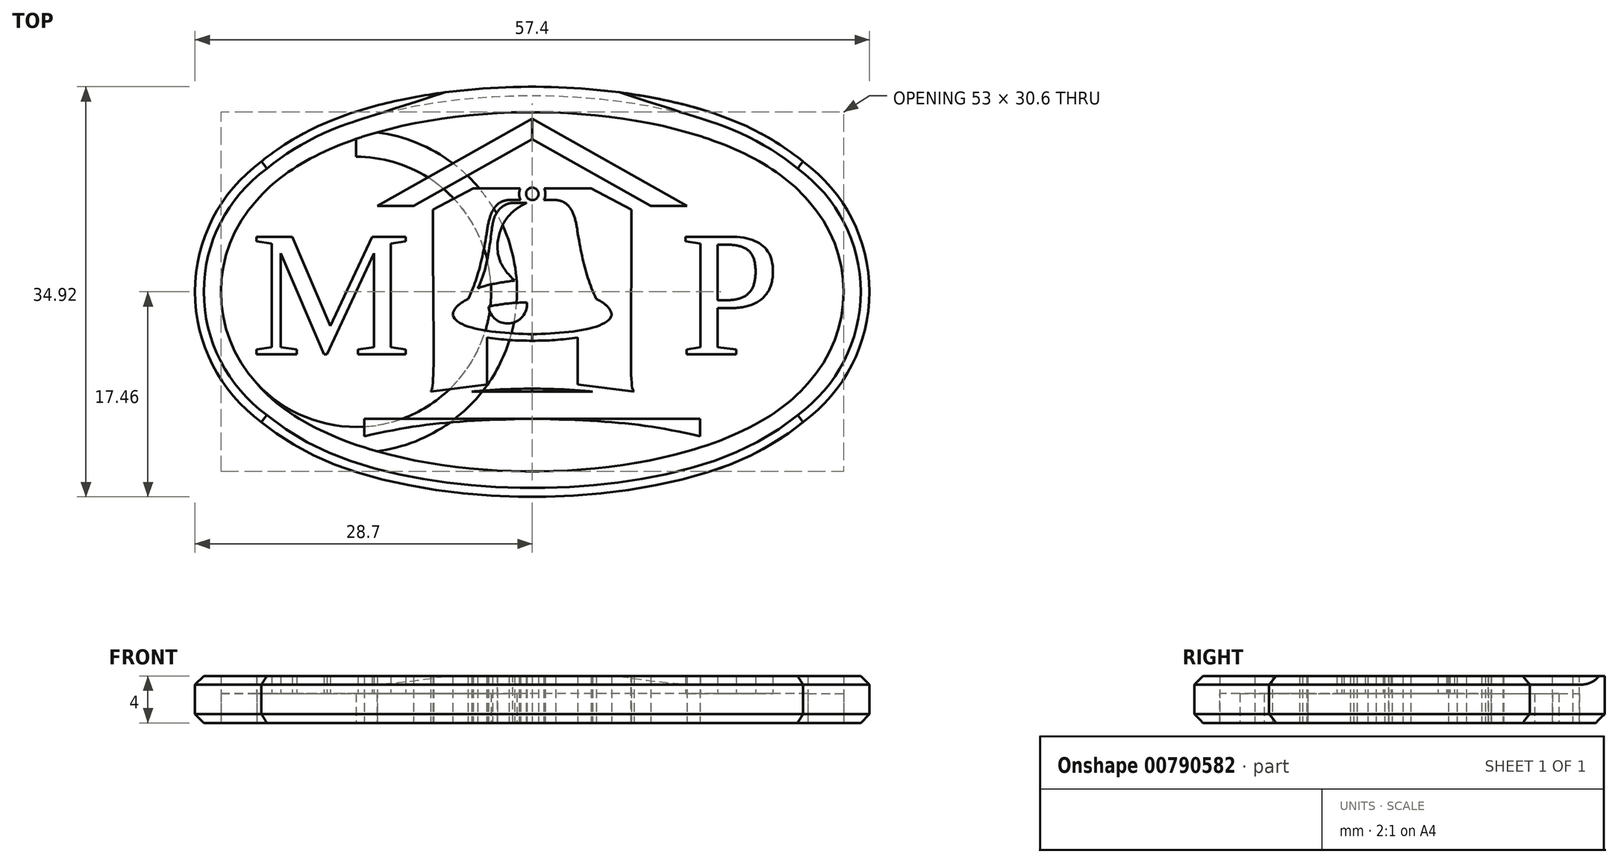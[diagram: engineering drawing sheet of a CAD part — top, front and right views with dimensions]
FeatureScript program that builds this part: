
annotation { "Feature Type Name" : "Feature", "Feature Type Description" : "" }
export const myFeature = defineFeature(function(context is Context, id is Id, definition is map)
    precondition{}
    {
        {
            var Q0;
            Q0=qCreatedBy(makeId("Top.planeOp"),FACE);
            var sketch = newSketch(context, id + "F0", { "sketchPlane" : qUnion([Q0])});
            skLineSegment(sketch, "E0", {"start": v(0, 0) * mm, "end": v(15, 0) * mm});
            skCircle(sketch, "E1", {"center": v(15, 0) * mm, "radius": 11.5 * mm});
            skCircle(sketch, "E2.MirrorC", {"center": v(-15, 0) * mm, "radius": 11.5 * mm});
            skLineSegment(sketch, "E3", {"start": v(15, 0) * mm, "end": v(15, -11.5) * mm});
            skLineSegment(sketch, "E4", {"start": v(15, 0) * mm, "end": v(15, 7.8) * mm});
            skLineSegment(sketch, "E5", {"start": v(15, 7.8) * mm, "end": v(23.45, 7.8) * mm});
            skLineSegment(sketch, "E6.MirrorCS", {"start": v(-15, 0) * mm, "end": v(-15, 7.8) * mm});
            skLineSegment(sketch, "E7.MirrorCS", {"start": v(-15, 7.8) * mm, "end": v(-23.45, 7.8) * mm});
            skLineSegment(sketch, "E8", {"start": v(15, 7.8) * mm, "end": v(15, 17.8) * mm});
            skLineSegment(sketch, "E9.MirrorCS", {"start": v(-15, 7.8) * mm, "end": v(-15, 17.8) * mm});
            skFitSpline(sketch, "E10", {"points": [v(23.45, 7.8) * mm, v(-23.45, 7.8) * mm], "startDerivative": vector(-25.35, 30) * mm, "endDerivative": vector(-25.35, -30) * mm});
            skFitSpline(sketch, "E11.MirrorCS", {"points": [v(23.45, -7.8) * mm, v(-23.45, -7.8) * mm], "startDerivative": vector(-25.35, -30) * mm, "endDerivative": vector(-25.35, 30) * mm});
            skFitSpline(sketch, "E12.0", {"points": [v(24.98, 9.1) * mm, v(24.36, 9.83) * mm, v(22.94, 11.18) * mm, v(19.56, 13.43) * mm, v(14.48, 15.51) * mm, v(7.47, 16.98) * mm, v(0, 17.46) * mm, v(-7.47, 16.98) * mm, v(-14.48, 15.51) * mm, v(-19.56, 13.43) * mm, v(-22.94, 11.18) * mm, v(-24.36, 9.83) * mm, v(-24.98, 9.1) * mm]});
            skFitSpline(sketch, "E13.0", {"points": [v(24.98, -9.1) * mm, v(24.36, -9.83) * mm, v(22.94, -11.18) * mm, v(19.56, -13.43) * mm, v(14.48, -15.51) * mm, v(7.47, -16.98) * mm, v(0, -17.46) * mm, v(-7.47, -16.98) * mm, v(-14.48, -15.51) * mm, v(-19.56, -13.43) * mm, v(-22.94, -11.18) * mm, v(-24.36, -9.83) * mm, v(-24.98, -9.1) * mm]});
            skCircle(sketch, "E14.0", {"center": v(-15, 0) * mm, "radius": 13.7 * mm});
            skCircle(sketch, "E15.0", {"center": v(15, 0) * mm, "radius": 13.7 * mm});
            skSolve(sketch);
        }
        {
            var Q0;
            {var subQ7=sQuery(id+"F0.wireOp",EDGE,"E12.0");var subQ8=sQuery(id+"F0.wireOp",EDGE,"E8");var subQ9=makeQuery(id+"F0.imprint","INTERSECT",VERTEX,{"derivedFrom":[subQ8,subQ7]});Q0=makeQuery(id+"F0.imprint","IMPRINT",FACE,{"disambiguationData":[TD([[makeQuery(id+"F0.imprint","IMPRINT",EDGE,{"disambiguationData":[TD([[subQ9,1.0]])],"derivedFrom":subQ8}),1.0]])]});}
            var Q1;
            {var subQ0=sQuery(id+"F0.wireOp",EDGE,"E10");var subQ3=sQuery(id+"F0.wireOp",EDGE,"E9.MirrorCS");var subQ4=makeQuery(id+"F0.imprint","INTERSECT",VERTEX,{"derivedFrom":[subQ3,subQ0]});Q1=makeQuery(id+"F0.imprint","IMPRINT",FACE,{"disambiguationData":[TD([[makeQuery(id+"F0.imprint","IMPRINT",EDGE,{"disambiguationData":[TD([[subQ4,-1.0]])],"derivedFrom":subQ3}),1.0]])]});}
            var Q2;
            {var subQ0=sQuery(id+"F0.wireOp",EDGE,"E12.0");var subQ1=sQuery(id+"F0.wireOp",EDGE,"E9.MirrorCS");var subQ2=makeQuery(id+"F0.imprint","INTERSECT",VERTEX,{"derivedFrom":[subQ1,subQ0]});Q2=makeQuery(id+"F0.imprint","IMPRINT",FACE,{"disambiguationData":[TD([[makeQuery(id+"F0.imprint","IMPRINT",EDGE,{"disambiguationData":[TD([[subQ2,1.0]])],"derivedFrom":subQ1}),1.0]])]});}
            var Q3;
            {var subQ0=sQuery(id+"F0.wireOp",EDGE,"E15.0");var subQ1=sQuery(id+"F0.wireOp",EDGE,"E11.MirrorCS");var subQ2=makeQuery(id+"F0.imprint","INTERSECT",VERTEX,{"derivedFrom":[subQ1,subQ0]});Q3=makeQuery(id+"F0.imprint","IMPRINT",FACE,{"disambiguationData":[TD([[makeQuery(id+"F0.imprint","IMPRINT",EDGE,{"disambiguationData":[TD([[subQ2,-1.0]])],"derivedFrom":subQ1}),1.0]])]});}
            var Q4;
            {var subQ5=sQuery(id+"F0.wireOp",EDGE,"E10");var subQ6=sQuery(id+"F0.wireOp",EDGE,"E8");var subQ7=makeQuery(id+"F0.imprint","INTERSECT",VERTEX,{"derivedFrom":[subQ6,subQ5]});Q4=makeQuery(id+"F0.imprint","IMPRINT",FACE,{"disambiguationData":[TD([[makeQuery(id+"F0.imprint","IMPRINT",EDGE,{"disambiguationData":[TD([[subQ7,-1.0]])],"derivedFrom":subQ6}),-1.0]])]});}
            var Q5;
            {var subQ0=sQuery(id+"F0.wireOp",EDGE,"E12.0");var subQ1=sQuery(id+"F0.wireOp",EDGE,"E8");var subQ2=makeQuery(id+"F0.imprint","INTERSECT",VERTEX,{"derivedFrom":[subQ1,subQ0]});Q5=makeQuery(id+"F0.imprint","IMPRINT",FACE,{"disambiguationData":[TD([[makeQuery(id+"F0.imprint","IMPRINT",EDGE,{"disambiguationData":[TD([[subQ2,1.0]])],"derivedFrom":subQ1}),-1.0]])]});}
            var Q6;
            {var subQ0=sQuery(id+"F0.wireOp",EDGE,"E10");var subQ1=sQuery(id+"F0.wireOp",EDGE,"E8");var subQ2=makeQuery(id+"F0.imprint","INTERSECT",VERTEX,{"derivedFrom":[subQ1,subQ0]});Q6=makeQuery(id+"F0.imprint","IMPRINT",FACE,{"disambiguationData":[TD([[makeQuery(id+"F0.imprint","IMPRINT",EDGE,{"disambiguationData":[TD([[subQ2,-1.0]])],"derivedFrom":subQ1}),1.0]])]});}
            var Q7;
            {var subQ0=sQuery(id+"F0.wireOp",EDGE,"E10");var subQ1=sQuery(id+"F0.wireOp",EDGE,"E9.MirrorCS");var subQ2=makeQuery(id+"F0.imprint","INTERSECT",VERTEX,{"derivedFrom":[subQ1,subQ0]});Q7=makeQuery(id+"F0.imprint","IMPRINT",FACE,{"disambiguationData":[TD([[makeQuery(id+"F0.imprint","IMPRINT",EDGE,{"disambiguationData":[TD([[subQ2,-1.0]])],"derivedFrom":subQ1}),-1.0]])]});}
            extrude(context, id + "F1", {"entities" : qUnion([Q0, Q1, Q2, Q3, Q4, Q5, Q6, Q7]), "depth" : 4 * mm, "offsetDistance" : 25 * mm});
        }
        {
            var Q0;
            {var subQ4=sQuery(id+"F0.wireOp",EDGE,"E7.MirrorCS");Q0=makeQuery(id+"F0.imprint","IMPRINT",FACE,{"disambiguationData":[TD([[makeQuery(id+"F0.imprint","IMPRINT",EDGE,{"derivedFrom":subQ4}),1.0]])]});}
            var Q1;
            {var subQ0=sQuery(id+"F0.wireOp",EDGE,"E7.MirrorCS");Q1=makeQuery(id+"F0.imprint","IMPRINT",FACE,{"disambiguationData":[TD([[makeQuery(id+"F0.imprint","IMPRINT",EDGE,{"derivedFrom":subQ0}),-1.0]])]});}
            var Q2;
            {var subQ1=sQuery(id+"F0.wireOp",EDGE,"E2.MirrorC");var subQ3=sQuery(id+"F0.wireOp",EDGE,"E9.MirrorCS");var subQ4=makeQuery(id+"F0.imprint","INTERSECT",VERTEX,{"derivedFrom":[subQ1,subQ3]});Q2=makeQuery(id+"F0.imprint","IMPRINT",FACE,{"disambiguationData":[TD([[makeQuery(id+"F0.imprint","IMPRINT",EDGE,{"disambiguationData":[TD([[subQ4,-1.0]])],"derivedFrom":subQ3}),1.0]])]});}
            var Q3;
            {var subQ5=sQuery(id+"F0.wireOp",EDGE,"E11.MirrorCS");var subQ7=sQuery(id+"F0.wireOp",EDGE,"E2.MirrorC");var subQ8=makeQuery(id+"F0.imprint","INTERSECT",VERTEX,{"derivedFrom":[subQ7,subQ5]});Q3=makeQuery(id+"F0.imprint","IMPRINT",FACE,{"disambiguationData":[TD([[makeQuery(id+"F0.imprint","IMPRINT",EDGE,{"disambiguationData":[TD([[subQ8,1.0]])],"derivedFrom":subQ7}),1.0]])]});}
            var Q4;
            {var subQ0=sQuery(id+"F0.wireOp",EDGE,"E15.0");var subQ2=sQuery(id+"F0.wireOp",EDGE,"E10");var subQ3=makeQuery(id+"F0.imprint","INTERSECT",VERTEX,{"derivedFrom":[subQ2,subQ0]});Q4=makeQuery(id+"F0.imprint","IMPRINT",FACE,{"disambiguationData":[TD([[makeQuery(id+"F0.imprint","IMPRINT",EDGE,{"disambiguationData":[TD([[subQ3,-1.0]])],"derivedFrom":subQ2}),1.0]])]});}
            var Q5;
            {var subQ3=sQuery(id+"F0.wireOp",EDGE,"E15.0");var subQ6=sQuery(id+"F0.wireOp",EDGE,"E0");var subQ9=makeQuery(id+"F0.imprint","INTERSECT",VERTEX,{"derivedFrom":[subQ6,subQ3]});Q5=makeQuery(id+"F0.imprint","IMPRINT",FACE,{"disambiguationData":[TD([[makeQuery(id+"F0.imprint","IMPRINT",EDGE,{"disambiguationData":[TD([[subQ9,-1.0]])],"derivedFrom":subQ6}),1.0]])]});}
            var Q6;
            {var subQ0=sQuery(id+"F0.wireOp",EDGE,"E4");Q6=makeQuery(id+"F0.imprint","IMPRINT",FACE,{"disambiguationData":[TD([[makeQuery(id+"F0.imprint","IMPRINT",EDGE,{"derivedFrom":subQ0}),1.0]])]});}
            var Q7;
            {var subQ0=sQuery(id+"F0.wireOp",EDGE,"E3");Q7=makeQuery(id+"F0.imprint","IMPRINT",FACE,{"disambiguationData":[TD([[makeQuery(id+"F0.imprint","IMPRINT",EDGE,{"derivedFrom":subQ0}),-1.0]])]});}
            var Q8;
            {var subQ3=sQuery(id+"F0.wireOp",EDGE,"E15.0");var subQ6=sQuery(id+"F0.wireOp",EDGE,"E0");var subQ8=makeQuery(id+"F0.imprint","INTERSECT",VERTEX,{"derivedFrom":[subQ6,subQ3]});Q8=makeQuery(id+"F0.imprint","IMPRINT",FACE,{"disambiguationData":[TD([[makeQuery(id+"F0.imprint","IMPRINT",EDGE,{"disambiguationData":[TD([[subQ8,-1.0]])],"derivedFrom":subQ6}),-1.0]])]});}
            var Q9;
            {var subQ0=sQuery(id+"F0.wireOp",EDGE,"E5");Q9=makeQuery(id+"F0.imprint","IMPRINT",FACE,{"disambiguationData":[TD([[makeQuery(id+"F0.imprint","IMPRINT",EDGE,{"derivedFrom":subQ0}),1.0]])]});}
            var Q10;
            {var subQ1=sQuery(id+"F0.wireOp",EDGE,"E1");var subQ3=sQuery(id+"F0.wireOp",EDGE,"E8");var subQ4=makeQuery(id+"F0.imprint","INTERSECT",VERTEX,{"derivedFrom":[subQ1,subQ3]});Q10=makeQuery(id+"F0.imprint","IMPRINT",FACE,{"disambiguationData":[TD([[makeQuery(id+"F0.imprint","IMPRINT",EDGE,{"disambiguationData":[TD([[subQ4,-1.0]])],"derivedFrom":subQ3}),-1.0]])]});}
            var Q11;
            {var subQ3=sQuery(id+"F0.wireOp",EDGE,"E3");Q11=makeQuery(id+"F0.imprint","IMPRINT",FACE,{"disambiguationData":[TD([[makeQuery(id+"F0.imprint","IMPRINT",EDGE,{"derivedFrom":subQ3}),1.0]])]});}
            extrude(context, id + "F2", {"entities" : qUnion([Q0, Q1, Q2, Q3, Q4, Q5, Q6, Q7, Q8, Q9, Q10, Q11]), "depth" : 2.5 * mm, "offsetDistance" : 25 * mm});
        }
        {
            var Q0;
            Q0=qCreatedBy(makeId("Top.planeOp"),FACE);
            var sketch = newSketch(context, id + "F3", { "sketchPlane" : qUnion([Q0])});
            skLineSegment(sketch, "E16", {"start": v(0, 0.7) * mm, "end": v(0, -12.3) * mm});
            skLineSegment(sketch, "E17", {"start": v(0, -12.3) * mm, "end": v(-14.29, -12.3) * mm});
            skLineSegment(sketch, "E18", {"start": v(0, 0.7) * mm, "end": v(0, -10.8) * mm});
            skLineSegment(sketch, "E19", {"start": v(0, -10.8) * mm, "end": v(-14.29, -10.8) * mm});
            skLineSegment(sketch, "E20", {"start": v(0, 0.7) * mm, "end": v(0, -8.5) * mm});
            skLineSegment(sketch, "E21", {"start": v(0, -8.5) * mm, "end": v(-8.65, -8.5) * mm});
            skLineSegment(sketch, "E22", {"start": v(0, 0.7) * mm, "end": v(0, -7.9) * mm});
            skLineSegment(sketch, "E23", {"start": v(0, -7.9) * mm, "end": v(-3.86, -7.9) * mm});
            skLineSegment(sketch, "E24", {"start": v(0, 0.7) * mm, "end": v(0, 7) * mm});
            skLineSegment(sketch, "E25", {"start": v(0, 7) * mm, "end": v(-8.45, 7) * mm});
            skLineSegment(sketch, "E26", {"start": v(0, 0.7) * mm, "end": v(0, 7.3) * mm});
            skLineSegment(sketch, "E27", {"start": v(0, 7.3) * mm, "end": v(-10.1, 7.3) * mm});
            skLineSegment(sketch, "E28", {"start": v(-10.1, 7.3) * mm, "end": v(-13.18, 7.3) * mm});
            skLineSegment(sketch, "E29", {"start": v(0, 0.7) * mm, "end": v(0, 8.8) * mm});
            skLineSegment(sketch, "E30", {"start": v(0, 8.8) * mm, "end": v(-5.02, 8.8) * mm});
            skLineSegment(sketch, "E31", {"start": v(-8.45, 7) * mm, "end": v(-5.02, 8.8) * mm});
            skFitSpline(sketch, "E32", {"points": [v(-14.29, -12.3) * mm, v(0, -10.8) * mm], "startDerivative": vector(14.64, 3.42) * mm, "endDerivative": vector(18.4, 0.45) * mm});
            skFitSpline(sketch, "E33", {"points": [v(-14.29, -10.8) * mm, v(0, -8.25) * mm], "startDerivative": vector(14.64, 6.22) * mm, "endDerivative": vector(14.96, 0.15) * mm});
            skCircle(sketch, "E34", {"center": v(0, 8.34) * mm, "radius": 0.53 * mm});
            skCircle(sketch, "E35.0", {"center": v(0, 8.34) * mm, "radius": 1.12 * mm});
            skLineSegment(sketch, "E36", {"start": v(-0.99, 7.81) * mm, "end": v(-1.98, 7.81) * mm});
            skFitSpline(sketch, "E37", {"points": [v(-1.98, 7.81) * mm, v(-3.88, 4.92) * mm], "startDerivative": vector(-3.62, -0.08) * mm, "endDerivative": vector(-0.56, -5.19) * mm});
            skFitSpline(sketch, "E38", {"points": [v(-3.88, 4.92) * mm, v(-5.46, -0.62) * mm], "startDerivative": vector(-1.23, -6.62) * mm, "endDerivative": vector(-2.61, -5.3) * mm});
            skFitSpline(sketch, "E39", {"points": [v(-5.46, -0.62) * mm, v(-6.75, -1.98) * mm], "startDerivative": vector(-2.25, -1.07) * mm, "endDerivative": vector(-0.05, -1.55) * mm});
            skFitSpline(sketch, "E40", {"points": [v(-6.75, -1.98) * mm, v(0, -3.6) * mm], "startDerivative": vector(0.7, -3.64) * mm, "endDerivative": vector(8.58, -0.1) * mm});
            skArc(sketch, "E41", {"start": v(-3.73, -1.26) * mm, "mid": v(-1.92, -2.7) * mm, "end": v(-0.45, -0.91) * mm});
            skFitSpline(sketch, "E42", {"points": [v(-3.73, -1.26) * mm, v(-0.45, -0.91) * mm], "startDerivative": vector(3.74, 0.72) * mm, "endDerivative": vector(3.71, -0.01) * mm});
            skLineSegment(sketch, "E43", {"start": v(-8.65, -8.5) * mm, "end": v(-3.86, -7.9) * mm});
            skLineSegment(sketch, "E44", {"start": v(-3.86, -3.9) * mm, "end": v(-3.86, -7.9) * mm});
            skFitSpline(sketch, "E45", {"points": [v(-3.86, -3.9) * mm, v(0, -4.17) * mm], "startDerivative": vector(4.02, -0.56) * mm, "endDerivative": vector(4.14, 0) * mm});
            skLineSegment(sketch, "E46", {"start": v(0, 14.75) * mm, "end": v(0, 13) * mm});
            skLineSegment(sketch, "E47", {"start": v(0, 13) * mm, "end": v(-10.1, 7.3) * mm});
            skLineSegment(sketch, "E48", {"start": v(-13.18, 7.3) * mm, "end": v(0, 14.75) * mm});
            skLineSegment(sketch, "E49", {"start": v(0, -3.6) * mm, "end": v(0, -4.17) * mm});
            skFitSpline(sketch, "E50", {"points": [v(-8.45, 7) * mm, v(-8.65, -8.5) * mm], "startDerivative": vector(-0.03, -32.53) * mm, "endDerivative": vector(-1.29, -0.72) * mm});
            skLineSegment(sketch, "E51", {"start": v(-14.29, -10.8) * mm, "end": v(-14.29, -12.3) * mm});
            skFitSpline(sketch, "E52", {"points": [v(-0.47, 7.58) * mm, v(-2.94, 4.18) * mm], "startDerivative": vector(-5.24, -2.54) * mm, "endDerivative": vector(-0.74, -4.51) * mm});
            skFitSpline(sketch, "E53", {"points": [v(-2.94, 4.18) * mm, v(-1.5, 0.96) * mm], "startDerivative": vector(-0.42, -4.51) * mm, "endDerivative": vector(2.55, -2.34) * mm});
            skLineSegment(sketch, "E54", {"start": v(-0.47, 7.58) * mm, "end": v(-1.65, 7.58) * mm});
            skFitSpline(sketch, "E55", {"points": [v(-1.65, 7.58) * mm, v(-3.38, 5.7) * mm], "startDerivative": vector(-2.7, -0.15) * mm, "endDerivative": vector(-0.37, -3.08) * mm});
            skFitSpline(sketch, "E56", {"points": [v(-3.38, 5.7) * mm, v(-4.64, 0.3) * mm], "startDerivative": vector(-0.42, -2.34) * mm, "endDerivative": vector(-2.82, -5.2) * mm});
            skFitSpline(sketch, "E57", {"points": [v(-4.64, 0.3) * mm, v(-1.5, 0.96) * mm], "startDerivative": vector(2.65, 1.05) * mm, "endDerivative": vector(3.25, 0.43) * mm});
            skSolve(sketch);
        }
        {
            var Q0;
            {var subQ1=sQuery(id+"F3.wireOp",EDGE,"E38");Q0=makeQuery(id+"F3.imprint","IMPRINT",FACE,{"disambiguationData":[TD([[makeQuery(id+"F3.imprint","IMPRINT",EDGE,{"derivedFrom":subQ1}),-1.0]])]});}
            var Q1;
            {var subQ0=sQuery(id+"F3.wireOp",EDGE,"E18");Q1=makeQuery(id+"F3.imprint","IMPRINT",FACE,{"disambiguationData":[TD([[makeQuery(id+"F3.imprint","IMPRINT",EDGE,{"derivedFrom":subQ0}),-1.0]])]});}
            var Q2;
            Q2=makeQuery(id+"F3.imprint","IMPRINT",FACE,{"disambiguationData":[TD([[makeQuery(id+"F3.imprint","IMPRINT",EDGE,{"derivedFrom":sQuery(id+"F3.wireOp",EDGE,"E19")}),1.0]])]});
            var Q3;
            Q3=makeQuery(id+"F3.imprint","IMPRINT",FACE,{"disambiguationData":[TD([[makeQuery(id+"F3.imprint","IMPRINT",EDGE,{"derivedFrom":sQuery(id+"F3.wireOp",EDGE,"E28")}),-1.0]])]});
            var Q4;
            {var subQ0=sQuery(id+"F3.wireOp",EDGE,"E36");Q4=makeQuery(id+"F3.imprint","IMPRINT",FACE,{"disambiguationData":[TD([[makeQuery(id+"F3.imprint","IMPRINT",EDGE,{"derivedFrom":subQ0}),-1.0]])]});}
            var Q5;
            {var subQ0=sQuery(id+"F3.wireOp",EDGE,"E31");var subQ5=sQuery(id+"F3.wireOp",EDGE,"E27");var subQ6=makeQuery(id+"F3.imprint","INTERSECT",VERTEX,{"derivedFrom":[subQ5,subQ0]});Q5=makeQuery(id+"F3.imprint","IMPRINT",FACE,{"disambiguationData":[TD([[makeQuery(id+"F3.imprint","IMPRINT",EDGE,{"disambiguationData":[TD([[subQ6,1.0]])],"derivedFrom":subQ5}),1.0]])]});}
            var Q6;
            {var subQ0=sQuery(id+"F3.wireOp",EDGE,"E30");var subQ1=sQuery(id+"F3.wireOp",EDGE,"E29");var subQ2=makeQuery(id+"F3.imprint","INTERSECT",VERTEX,{"derivedFrom":[subQ1,subQ0]});Q6=makeQuery(id+"F3.imprint","IMPRINT",FACE,{"disambiguationData":[TD([[makeQuery(id+"F3.imprint","IMPRINT",EDGE,{"disambiguationData":[TD([[subQ2,1.0]])],"derivedFrom":subQ1}),1.0]])]});}
            var Q7;
            {var subQ0=sQuery(id+"F3.wireOp",EDGE,"E30");var subQ1=sQuery(id+"F3.wireOp",EDGE,"E29");var subQ2=makeQuery(id+"F3.imprint","INTERSECT",VERTEX,{"derivedFrom":[subQ1,subQ0]});Q7=makeQuery(id+"F3.imprint","IMPRINT",FACE,{"disambiguationData":[TD([[makeQuery(id+"F3.imprint","IMPRINT",EDGE,{"disambiguationData":[TD([[subQ2,1.0]])],"derivedFrom":subQ1}),-1.0]])]});}
            var Q8;
            {var subQ1=sQuery(id+"F3.wireOp",EDGE,"E20");var subQ3=sQuery(id+"F3.wireOp",EDGE,"E33");var subQ4=makeQuery(id+"F3.imprint","INTERSECT",VERTEX,{"derivedFrom":[subQ1,subQ3]});Q8=makeQuery(id+"F3.imprint","IMPRINT",FACE,{"disambiguationData":[TD([[makeQuery(id+"F3.imprint","IMPRINT",EDGE,{"disambiguationData":[TD([[subQ4,1.0]])],"derivedFrom":subQ3}),-1.0]])]});}
            extrude(context, id + "F4", {"entities" : qUnion([Q0, Q1, Q2, Q3, Q4, Q5, Q6, Q7, Q8]), "depth" : 4 * mm, "offsetDistance" : 25 * mm});
        }
        {
            var Q0;
            Q0=makeQuery(id+"F4.opExtrude","SWEPT_BODY",BODY,{"disambiguationData":[OSD([sQuery(id+"F3.wireOp",EDGE,"E30"),sQuery(id+"F3.wireOp",EDGE,"E31"),sQuery(id+"F3.wireOp",EDGE,"E35.0"),sQuery(id+"F3.wireOp",EDGE,"E36"),sQuery(id+"F3.wireOp",EDGE,"E37"),sQuery(id+"F3.wireOp",EDGE,"E38"),sQuery(id+"F3.wireOp",EDGE,"E39"),sQuery(id+"F3.wireOp",EDGE,"E40"),sQuery(id+"F3.wireOp",EDGE,"E43"),sQuery(id+"F3.wireOp",EDGE,"E44"),sQuery(id+"F3.wireOp",EDGE,"E45"),sQuery(id+"F3.wireOp",EDGE,"E49"),sQuery(id+"F3.wireOp",EDGE,"E50")])]});
            var Q1;
            Q1=makeQuery(id+"F4.opExtrude","SWEPT_BODY",BODY,{"disambiguationData":[OSD([sQuery(id+"F3.wireOp",EDGE,"E18"),sQuery(id+"F3.wireOp",EDGE,"E21"),sQuery(id+"F3.wireOp",EDGE,"E32"),sQuery(id+"F3.wireOp",EDGE,"E33"),sQuery(id+"F3.wireOp",EDGE,"E51")])]});
            var Q2;
            Q2=makeQuery(id+"F4.opExtrude","SWEPT_BODY",BODY,{"disambiguationData":[OSD([sQuery(id+"F3.wireOp",EDGE,"E28"),sQuery(id+"F3.wireOp",EDGE,"E46"),sQuery(id+"F3.wireOp",EDGE,"E47"),sQuery(id+"F3.wireOp",EDGE,"E48")])]});
            var Q3;
            Q3=qCreatedBy(makeId("Right.planeOp"),FACE);
            mirror(context, id + "F5", {"entities" : qUnion([Q0, Q1, Q2]), "mirrorPlane" : qUnion([Q3])});
        }
        {
            var Q0;
            Q0=makeQuery(id+"F3.imprint","IMPRINT",FACE,{"disambiguationData":[TD([[makeQuery(id+"F3.imprint","IMPRINT",EDGE,{"derivedFrom":sQuery(id+"F3.wireOp",EDGE,"E41")}),1.0]])]});
            extrude(context, id + "F6", {"entities" : qUnion([Q0]), "depth" : 4 * mm, "offsetDistance" : 25 * mm});
        }
        {
            var Q0;
            {var subQ4=sQuery(id+"F3.wireOp",EDGE,"E53");Q0=makeQuery(id+"F3.imprint","IMPRINT",FACE,{"disambiguationData":[TD([[makeQuery(id+"F3.imprint","IMPRINT",EDGE,{"derivedFrom":subQ4}),-1.0]])]});}
            var Q1;
            {var subQ0=sQuery(id+"F3.wireOp",EDGE,"E52");var subQ1=sQuery(id+"F3.wireOp",EDGE,"E25");var subQ2=makeQuery(id+"F3.imprint","INTERSECT",VERTEX,{"derivedFrom":[subQ1,subQ0]});Q1=makeQuery(id+"F3.imprint","IMPRINT",FACE,{"disambiguationData":[TD([[makeQuery(id+"F3.imprint","IMPRINT",EDGE,{"disambiguationData":[TD([[subQ2,-1.0]])],"derivedFrom":subQ1}),-1.0]])]});}
            var Q2;
            {var subQ5=sQuery(id+"F3.wireOp",EDGE,"E52");var subQ6=sQuery(id+"F3.wireOp",EDGE,"E27");var subQ7=makeQuery(id+"F3.imprint","INTERSECT",VERTEX,{"derivedFrom":[subQ6,subQ5]});Q2=makeQuery(id+"F3.imprint","IMPRINT",FACE,{"disambiguationData":[TD([[makeQuery(id+"F3.imprint","IMPRINT",EDGE,{"disambiguationData":[TD([[subQ7,-1.0]])],"derivedFrom":subQ6}),-1.0]])]});}
            var Q3;
            {var subQ0=sQuery(id+"F3.wireOp",EDGE,"E54");var subQ1=sQuery(id+"F3.wireOp",EDGE,"E35.0");var subQ2=makeQuery(id+"F3.imprint","INTERSECT",VERTEX,{"derivedFrom":[subQ1,subQ0]});Q3=makeQuery(id+"F3.imprint","IMPRINT",FACE,{"disambiguationData":[TD([[makeQuery(id+"F3.imprint","IMPRINT",EDGE,{"disambiguationData":[TD([[subQ2,-1.0]])],"derivedFrom":subQ1}),1.0]])]});}
            extrude(context, id + "F7", {"entities" : qUnion([Q0, Q1, Q2, Q3]), "depth" : 4 * mm, "offsetDistance" : 25 * mm});
        }
        {
            var Q0;
            Q0=qCreatedBy(makeId("Top.planeOp"),FACE);
            var sketch = newSketch(context, id + "F8", { "sketchPlane" : qUnion([Q0])});
            skText(sketch, "E58", { "text": "M      P", "fontName": "Tinos-Regular.ttf"});
            const initialGuessF8  = {"E58": [-0.0239, -0.00531, 1, 0, 0.011]};
            skSetInitialGuess(sketch, initialGuessF8);
            skSolve(sketch);
        }
        {
            var Q0;
            Q0 = qSketchRegion(id + "F8", true);
            extrude(context, id + "F9", {"entities" : qUnion([Q0]), "operationType" : NewBodyOperationType.ADD, "depth" : 4 * mm, "offsetDistance" : 25 * mm});
        }
        {
            var Q0;
            Q0=makeQuery(id+"F1.opExtrude","CAP_EDGE",EDGE,{"disambiguationData":[OSD([sQuery(id+"F0.wireOp",EDGE,"E13.0")])],"isStart":false});
            var Q1;
            Q1=makeQuery(id+"F1.opExtrude","CAP_EDGE",EDGE,{"disambiguationData":[OSD([sQuery(id+"F0.wireOp",EDGE,"E14.0")])],"isStart":false});
            var Q2;
            Q2=makeQuery(id+"F1.opExtrude","CAP_EDGE",EDGE,{"disambiguationData":[OSD([sQuery(id+"F0.wireOp",EDGE,"E15.0")])],"isStart":false});
            var Q3;
            Q3=makeQuery(id+"F1.opExtrude","CAP_EDGE",EDGE,{"disambiguationData":[OSD([sQuery(id+"F0.wireOp",EDGE,"E13.0")])],"isStart":true});
            var Q4;
            Q4=makeQuery(id+"F1.opExtrude","CAP_EDGE",EDGE,{"disambiguationData":[OSD([sQuery(id+"F0.wireOp",EDGE,"E15.0")])],"isStart":true});
            var Q5;
            Q5=makeQuery(id+"F1.opExtrude","CAP_EDGE",EDGE,{"disambiguationData":[OSD([sQuery(id+"F0.wireOp",EDGE,"E14.0")])],"isStart":true});
            var Q6;
            Q6=makeQuery(id+"F1.opExtrude","CAP_EDGE",EDGE,{"disambiguationData":[OSD([sQuery(id+"F0.wireOp",EDGE,"E12.0")])],"isStart":true});
            chamfer(context, id + "F10", {"entities" : qUnion([Q0, Q1, Q2, Q3, Q4, Q5, Q6]), "width" : .75 * mm, "tangentPropagation" : true});
        }
    });
